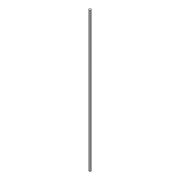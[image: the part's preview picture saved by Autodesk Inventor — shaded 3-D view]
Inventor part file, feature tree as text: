
AUTODESK INVENTOR PART (.ipt)
format: ipt  version: 2017 (Build 210142000, 142)  size: 69,120 bytes
history: native  units: in
note: dims shown in document units (in); Inventor stores cm internally (conversion verified against a paired STEP export)
features: extrude x1, thread x1, sketch x1
ambient origin geometry x8: Origin, YZ Plane, XZ Plane, XY Plane, X Axis, Y Axis, Z Axis, Center Point
bodies: Solid1 (feature_tree)
feature tree (3):
  extrude  "Extrusion1"  Depth=19.685in TaperAngle=0.0deg
  thread  "Thread1"  [1 undecoded]
  sketch  "Sketch1"  dims[d0=0.315in d1=19.685in d2=0.0in d3=1.0in d4=0.0in]
note: 1 required parameter value undecoded (feature->parameter linkage not recoverable at this tier; creation-order binding heuristic only, values carry confidence <= 0.55)
